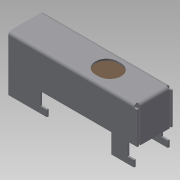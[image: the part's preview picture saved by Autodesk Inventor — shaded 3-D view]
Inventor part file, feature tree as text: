
AUTODESK INVENTOR PART (.ipt)
format: ipt  version: 2014 (Build 180170000, 170)  size: 199,168 bytes
history: native  units: mm
features: sheet_metal_op x7, sketch x5, reference x5, other x3, extrude x2, fillet x2, plane x1, chamfer x1
ambient origin geometry x8: Origin, YZ Plane, XZ Plane, XY Plane, X Axis, Y Axis, Z Axis, Center Point
bodies: Solid1 (feature_tree)
feature tree (26):
  plane  "Work Plane1"
  sheet_metal_op  "Face1"
  sheet_metal_op  "Flange1"
  sketch  "Sketch3"  dims[d4=1.0mm]
  sheet_metal_op  "Flange2"
  extrude  "Extrusion1"  Depth=0.5mm
  extrude  "Extrusion5"  Depth=0.5mm
  chamfer  "Chamfer1"  Distance=17.0mm Angle=90.0deg
  fillet  "Fillet1"  Radius=2.0mm
  fillet  "Fillet2"  Radius=0.5mm
  sketch  "Sketch1"  dims[d0=7.0mm d1=0.5mm]
  reference  "Reference1"
  reference  "Reference2"
  reference  "Reference3"
  reference  "Reference4"
  reference  "Reference5"
  other  "Plate1"
  sketch  "Sketch2"  dims[d2=0.5mm d3=0.25mm]
  other  "Plate2"
  sheet_metal_op  "Bend1"
  sheet_metal_op  "Corner1"
  sketch  "Sketch4"  dims[d5=0.5mm d6=17.0mm d7=90.0deg d8=0.5mm d9=2.0mm d10=0.5mm]
  other  "Plate3"
  sheet_metal_op  "Bend2"
  sheet_metal_op  "Corner2"
  sketch  "Sketch8"  dims[d11=0.5mm d13=20.0mm d14=0.5mm d15=0.25mm d16=1.0mm d17=0.5mm d18=11.0mm d19=90.0deg d20=0.5mm d21=2.0mm d22=0.5mm d23=0.5mm d24=15.0mm d25=0.0mm d28=3.0mm d32=40.0mm d37=6.0mm d38=4.0mm d39=3.0mm d40=5.0mm d41=2.0mm d42=2.0mm d43=1.0mm d44=7.0mm d45=1.0mm d46=14.0mm d47=0.0mm d48=1.5mm d49=2.0mm d50=45.0deg d51=0.5mm d52=0.5mm]
